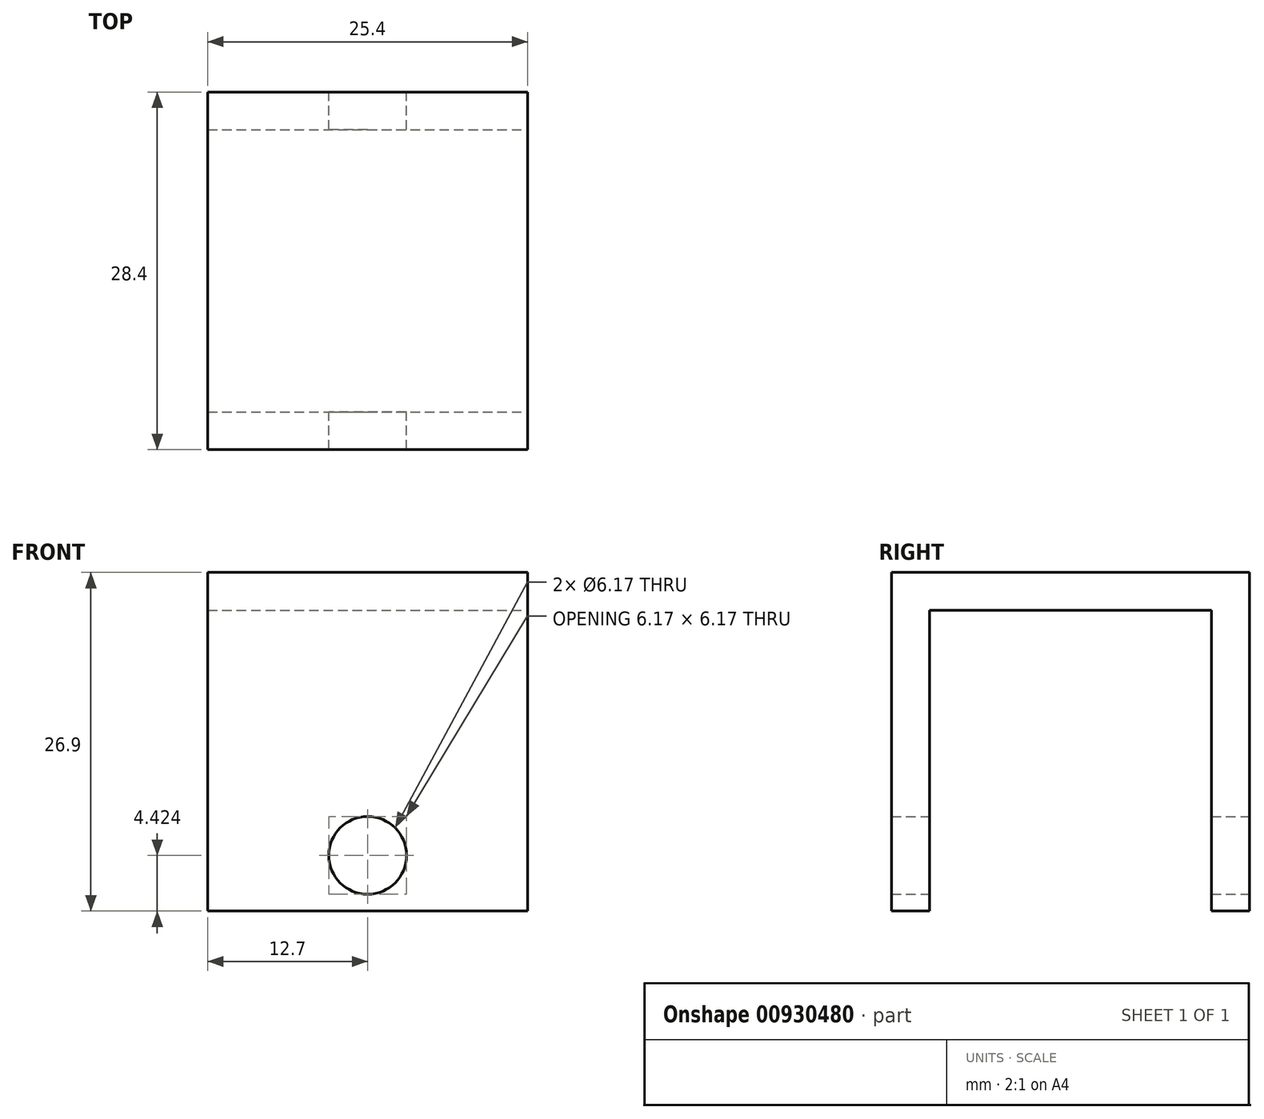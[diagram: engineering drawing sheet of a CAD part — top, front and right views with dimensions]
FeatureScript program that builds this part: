
annotation { "Feature Type Name" : "Feature", "Feature Type Description" : "" }
export const myFeature = defineFeature(function(context is Context, id is Id, definition is map)
    precondition{}
    {
        {
            var Q0;
            Q0=qCreatedBy(makeId("Right.planeOp"),FACE);
            var sketch = newSketch(context, id + "F0", { "sketchPlane" : qUnion([Q0])});
            skLineSegment(sketch, "E0", {"start": v(0, 0) * mm, "end": v(0, 25.4) * mm});
            skLineSegment(sketch, "E1", {"start": v(0, 25.4) * mm, "end": v(25.4, 25.4) * mm});
            skLineSegment(sketch, "E2", {"start": v(25.4, 25.4) * mm, "end": v(25.4, 25.4) * mm});
            skLineSegment(sketch, "E3", {"start": v(25.4, 25.4) * mm, "end": v(25.4, 0) * mm});
            skSolve(sketch);
        }
        {
            var Q0;
            Q0=qCreatedBy(makeId("Top.planeOp"),FACE);
            var sketch = newSketch(context, id + "F1", { "sketchPlane" : qUnion([Q0])});
            skLineSegment(sketch, "E4.bottom", {"start": v(12.7, -1.5) * mm, "end": v(-12.7, -1.5) * mm});
            skLineSegment(sketch, "E4.top", {"start": v(12.7, 1.5) * mm, "end": v(-12.7, 1.5) * mm});
            skLineSegment(sketch, "E4.left", {"start": v(12.7, -1.5) * mm, "end": v(12.7, 1.5) * mm});
            skLineSegment(sketch, "E4.right", {"start": v(-12.7, -1.5) * mm, "end": v(-12.7, 1.5) * mm});
            skPoint(sketch, "E4.middle", {"position": v(0, 0) * mm});
            skSolve(sketch);
        }
        {
            var Q0;
            Q0=makeQuery(id+"F1.imprint","IMPRINT",FACE,{"disambiguationData":[TD([[makeQuery(id+"F1.imprint","IMPRINT",EDGE,{"derivedFrom":sQuery(id+"F1.wireOp",EDGE,"E4.bottom")}),-1.0]])]});
            var Q1;
            Q1=sQuery(id+"F0.wireOp",EDGE,"E0");
            var Q2;
            Q2=sQuery(id+"F0.wireOp",EDGE,"E1");
            var Q3;
            Q3=sQuery(id+"F0.wireOp",EDGE,"E3");
            sweep(context, id + "F2", {"profiles" : qUnion([Q0]), "path" : qUnion([Q1, Q2, Q3])});
        }
        {
            var Q0;
            Q0=makeQuery(id+"F2.opSweep","SWEPT_FACE",FACE,{"disambiguationData":[OSD([sQuery(id+"F0.wireOp",EDGE,"E3"),sQuery(id+"F1.wireOp",EDGE,"E4.bottom")])]});
            var sketch = newSketch(context, id + "F3", { "sketchPlane" : qUnion([Q0])});
            skCircle(sketch, "E5", {"center": v(0, 4.42) * mm, "radius": 3.09 * mm});
            skSolve(sketch);
        }
        {
            var Q0;
            Q0=makeQuery(id+"F3.imprint","IMPRINT",FACE,{"disambiguationData":[TD([[makeQuery(id+"F3.imprint","IMPRINT",EDGE,{"derivedFrom":sQuery(id+"F3.wireOp",EDGE,"E5")}),1.0]])]});
            extrude(context, id + "F4", {"entities" : qUnion([Q0]), "operationType" : NewBodyOperationType.REMOVE, "oppositeDirection" : true, "depth" : 48.38 * mm, "offsetDistance" : 25.4 * mm});
        }
    });
